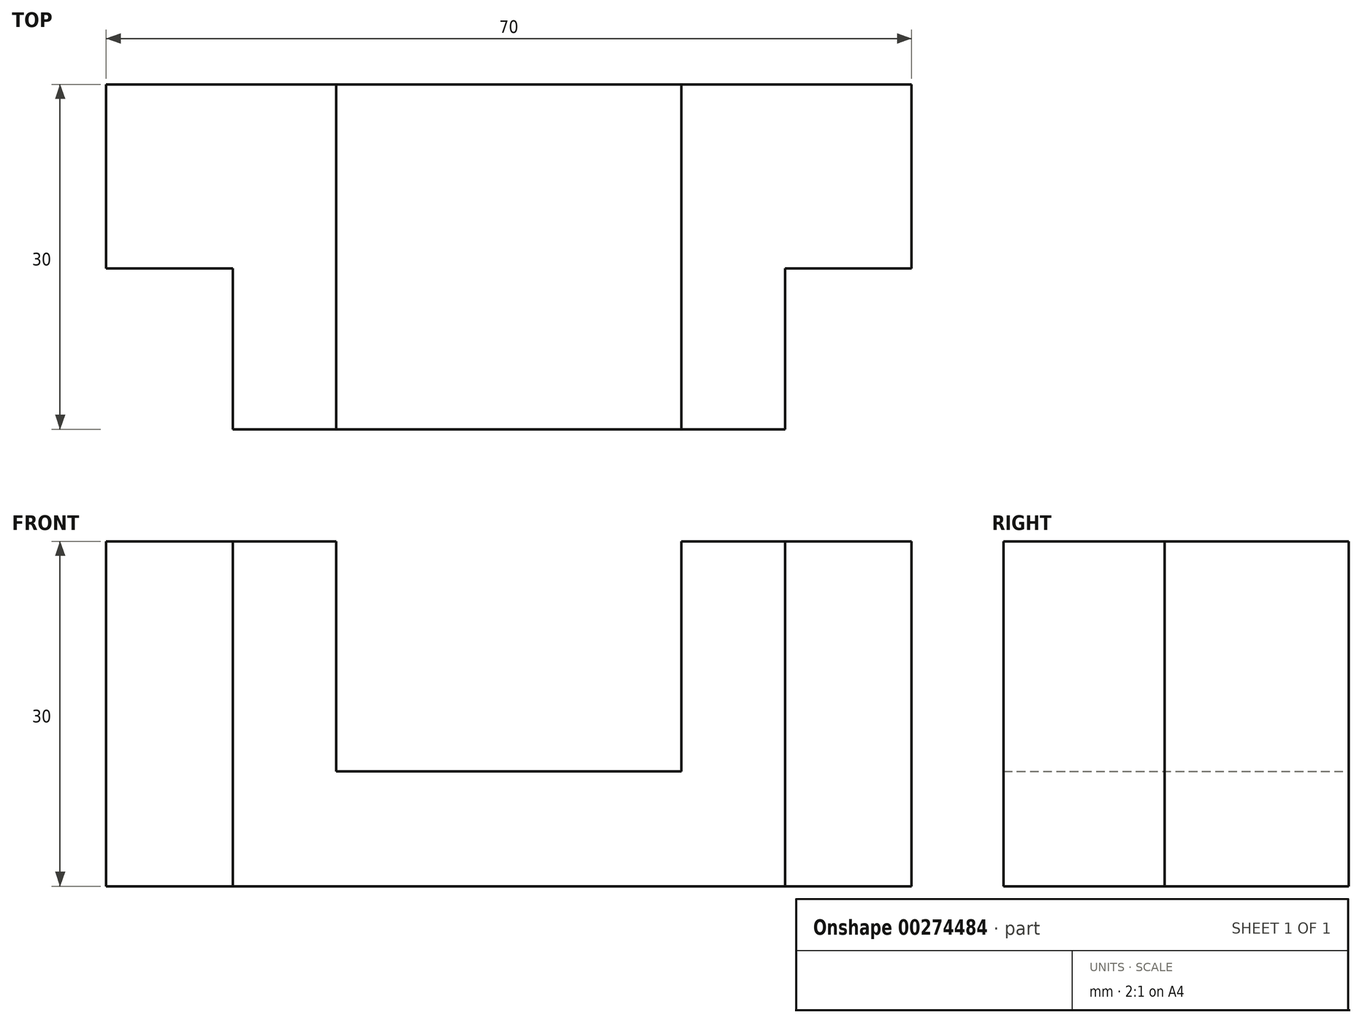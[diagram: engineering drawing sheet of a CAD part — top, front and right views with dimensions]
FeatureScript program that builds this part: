
annotation { "Feature Type Name" : "Feature", "Feature Type Description" : "" }
export const myFeature = defineFeature(function(context is Context, id is Id, definition is map)
    precondition{}
    {
        {
            var Q0;
            Q0=qCreatedBy(makeId("Front.planeOp"),FACE);
            var sketch = newSketch(context, id + "F0", { "sketchPlane" : qUnion([Q0])});
            skLineSegment(sketch, "E0.top", {"start": v(-24, -15) * mm, "end": v(24, -15) * mm});
            skLineSegment(sketch, "E0.left", {"start": v(-24, 15) * mm, "end": v(-24, -15) * mm});
            skLineSegment(sketch, "E0.right", {"start": v(24, 15) * mm, "end": v(24, -15) * mm});
            skLineSegment(sketch, "E1.top", {"start": v(-15, -5) * mm, "end": v(15, -5) * mm});
            skLineSegment(sketch, "E1.left", {"start": v(-15, 15) * mm, "end": v(-15, -5) * mm});
            skLineSegment(sketch, "E1.right", {"start": v(15, 15) * mm, "end": v(15, -5) * mm});
            skLineSegment(sketch, "E2.trimOffspring", {"start": v(15, 15) * mm, "end": v(24, 15) * mm});
            skLineSegment(sketch, "E3", {"start": v(-24, 15) * mm, "end": v(-15, 15) * mm});
            skLineSegment(sketch, "E4.bottom", {"start": v(24, 15) * mm, "end": v(35, 15) * mm});
            skLineSegment(sketch, "E4.top", {"start": v(24, -15) * mm, "end": v(35, -15) * mm});
            skLineSegment(sketch, "E4.right", {"start": v(35, 15) * mm, "end": v(35, -15) * mm});
            skLineSegment(sketch, "E5.bottom", {"start": v(-24, 15) * mm, "end": v(-35, 15) * mm});
            skLineSegment(sketch, "E5.top", {"start": v(-24, -15) * mm, "end": v(-35, -15) * mm});
            skLineSegment(sketch, "E5.right", {"start": v(-35, 15) * mm, "end": v(-35, -15) * mm});
            skSolve(sketch);
        }
        {
            var Q0;
            Q0=makeQuery(id+"F0.imprint","IMPRINT",FACE,{"disambiguationData":[TD([[makeQuery(id+"F0.imprint","IMPRINT",EDGE,{"derivedFrom":sQuery(id+"F0.wireOp",EDGE,"E0.top")}),1.0]])]});
            extrude(context, id + "F1", {"entities" : qUnion([Q0]), "depth" : 30 * mm});
        }
        {
            var Q0;
            Q0=makeQuery(id+"F0.imprint","IMPRINT",FACE,{"disambiguationData":[TD([[makeQuery(id+"F0.imprint","IMPRINT",EDGE,{"derivedFrom":sQuery(id+"F0.wireOp",EDGE,"E5.bottom")}),1.0]])]});
            var Q1;
            Q1=makeQuery(id+"F0.imprint","IMPRINT",FACE,{"disambiguationData":[TD([[makeQuery(id+"F0.imprint","IMPRINT",EDGE,{"derivedFrom":sQuery(id+"F0.wireOp",EDGE,"E4.bottom")}),-1.0]])]});
            extrude(context, id + "F2", {"entities" : qUnion([Q0, Q1]), "operationType" : NewBodyOperationType.ADD, "depth" : 16 * mm});
        }
    });
